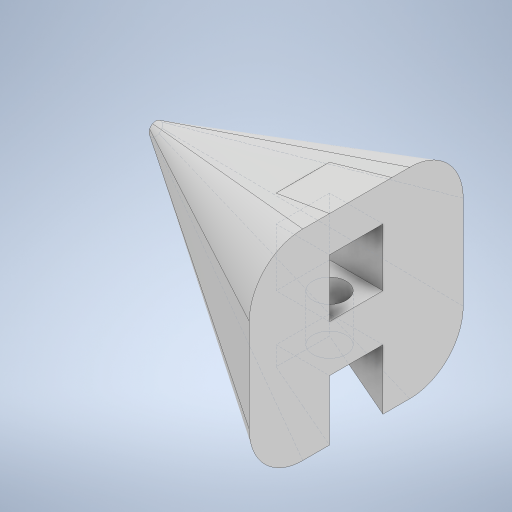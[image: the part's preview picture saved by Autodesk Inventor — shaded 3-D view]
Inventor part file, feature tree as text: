
AUTODESK INVENTOR PART (.ipt)
format: ipt  version: 2024 (Build 280153000, 153)  size: 672,256 bytes
history: native  units: mm
features: sketch x34, extrude x28, plane x4, chamfer x3, split x3, move_body x3, delete_face x1, fillet x1, boolean_combine x1, loft x1, other x1
ambient origin geometry x8: Origin, YZ Plane, XZ Plane, XY Plane, X Axis, Y Axis, Z Axis, Center Point
bodies: Solid1 (feature_tree), Solid2 (feature_tree), Solid3 (feature_tree), Solid4 (feature_tree), Solid5 (feature_tree), Solid6 (feature_tree), Solid7 (feature_tree)
feature tree (80):
  extrude  "Extrusion1"  Depth=16.0mm
  sketch  "Sketch2"  dims[d2=15.0mm d3=0.0mm d4=10.0mm]
  extrude  "Extrusion2"  Depth=10.0mm
  chamfer  "Chamfer1"  Distance=21.25mm
  extrude  "Extrusion3"  Depth=10.0mm TaperAngle=0.0deg
  extrude  "Extrusion4"  Depth=7.0mm TaperAngle=0.0deg
  extrude  "Extrusion5"  Depth=6.0mm TaperAngle=0.0deg
  chamfer  "Chamfer2"  Distance=6.0mm Angle=45.0deg
  sketch  "Sketch6"  dims[d14=7.0mm d15=11.5mm d16=0.0mm]
  extrude  "Extrusion6"  Depth=15.0mm
  extrude  "Extrusion7"  Depth=45.25mm TaperAngle=0.0deg
  chamfer  "Chamfer3"  Distance=11.5mm Angle=45.0deg
  sketch  "Sketch9"  dims[d26=3.3mm d27=45.25mm d28=0.0mm d29=11.5mm d30=5.5mm d31=45.0deg]
  extrude  "Extrusion8"  Depth=65.75mm TaperAngle=0.0deg
  extrude  "Extrusion9"  Depth=9.0mm TaperAngle=0.0deg
  extrude  "Extrusion10"  Depth=13.0mm TaperAngle=0.0deg
  sketch  "Sketch13"  dims[d43=24.0mm d44=21.0mm d45=0.0mm]
  extrude  "Extrusion11"  Depth=21.0mm TaperAngle=0.0deg
  extrude  "Extrusion12"  TaperAngle=0.0deg  [1 undecoded]
  extrude  "Extrusion13"  Depth=4.0mm
  plane  "Work Plane1"
  split  "Split1"
  move_body  "Move Body1"
  extrude  "Extrusion14"  Depth=1.0mm
  delete_face  "Delete Face1"
  fillet  "Fillet1"  Radius=1.5mm
  extrude  "Extrusion17"  Depth=1.0mm
  extrude  "Extrusion18"  Depth=1.2mm TaperAngle=0.0deg
  extrude  "Extrusion19"  [1 undecoded]
  extrude  "Extrusion20"  Depth=3.0mm TaperAngle=0.0deg
  plane  "Work Plane2"
  split  "Split2"
  move_body  "Move Body2"
  extrude  "Extrusion21"  Depth=15.0mm
  boolean_combine  "Combine1"
  plane  "Work Plane3"
  sketch  "Sketch26"  dims[d85=-15.0mm d86=-10.0mm d87=0.0mm d88=0.0mm]
  loft  "Loft1"
  plane  "Work Plane4"
  split  "Split3"
  move_body  "Move Body3"
  extrude  "Extrusion22"  TaperAngle=0.0deg  [1 undecoded]
  extrude  "Extrusion23"  Depth=4.0mm
  extrude  "Extrusion24"  Depth=4.0mm
  sketch  "Sketch31"  dims[d100=4.0mm d101=0.0mm d102=0.75mm d103=0.0mm]
  sketch  "Sketch32"  dims[d104=5.25mm d105=0.0mm d106=1.0mm]
  extrude  "Extrusion25"  Depth=4.0mm
  extrude  "Extrusion26"  Depth=2.0mm
  extrude  "Extrusion27"  Depth=4.0mm TaperAngle=0.0deg
  extrude  "Extrusion28"  Depth=1.0mm
  extrude  "Extrusion29"  Depth=4.0mm TaperAngle=0.0deg
  extrude  "Extrusion30"  Depth=4.0mm TaperAngle=0.0deg
  sketch  "Sketch1"  dims[d0=36.0mm d1=16.0mm]
  sketch  "Sketch3"  dims[d5=10.0mm]
  sketch  "Sketch4"  dims[d6=3.3mm d7=21.25mm d8=0.0mm]
  sketch  "Sketch5"  dims[d9=10.0mm d10=5.5mm d11=45.0deg d12=10.0mm d13=0.0mm]
  sketch  "Sketch7"  dims[d17=3.3mm d18=1.0mm d19=0.0mm d20=6.0mm d21=11.5mm d22=45.0deg]
  sketch  "Sketch8"  dims[d23=15.0mm d24=0.0mm d25=9.0mm]
  sketch  "Sketch10"  dims[d32=2.0mm d33=65.75mm d34=0.0mm]
  sketch  "Sketch11"  dims[d35=0.5mm d36=0.0mm d37=9.0mm d38=0.0mm]
  sketch  "Sketch12"  dims[d39=0.5mm d40=0.0mm d41=13.0mm d42=0.0mm]
  sketch  "Sketch14"  dims[d46=12.25mm d47=-12.0mm d48=0.0mm d49=0.0mm]
  sketch  "Sketch15"  dims[d50=10.0mm d51=0.0mm d52=4.0mm]
  sketch  "Sketch16"  dims[d61=1.0mm d62=1.0mm d63=1.5mm d64=0.0mm]
  sketch  "Sketch17"  dims[d65=1.0mm d66=1.0mm]
  sketch  "Sketch20"  dims[d67=5.5mm d68=0.0mm d69=1.2mm d70=0.0mm]
  sketch  "Sketch21"  dims[d71=2.2mm d72=0.0mm d73=-5.5mm]
  sketch  "Sketch22"  dims[d74=-3.0mm d75=0.0mm d76=0.0mm d77=3.0mm d78=0.0mm]
  sketch  "Sketch23"  dims[d79=15.0mm d80=1.0mm]
  sketch  "Sketch24"  dims[d81=0.0mm d82=90.0deg d83=0.0mm d84=90.0deg]
  sketch  "Sketch27"  dims[d89=4.0mm d90=11.0mm]
  other  "Edges1"
  sketch  "Sketch28"  dims[d91=4.0mm d92=0.0mm d93=4.0mm]
  sketch  "Sketch29"  dims[d94=4.0mm d95=0.0mm d96=2.5mm]
  sketch  "Sketch30"  dims[d97=12.0mm d98=0.0mm d99=2.0mm]
  sketch  "Sketch33"  dims[d107=4.0mm d108=0.0mm d109=5.75mm d110=0.0mm]
  sketch  "Sketch34"  dims[d111=1.5mm d112=4.0mm d113=0.0mm]
  sketch  "Sketch35"  dims[d53=0.872665mm]
  sketch  "Sketch36"
  sketch  "Sketch37"
note: 3 required parameter values undecoded (feature->parameter linkage not recoverable at this tier; creation-order binding heuristic only, values carry confidence <= 0.55)
